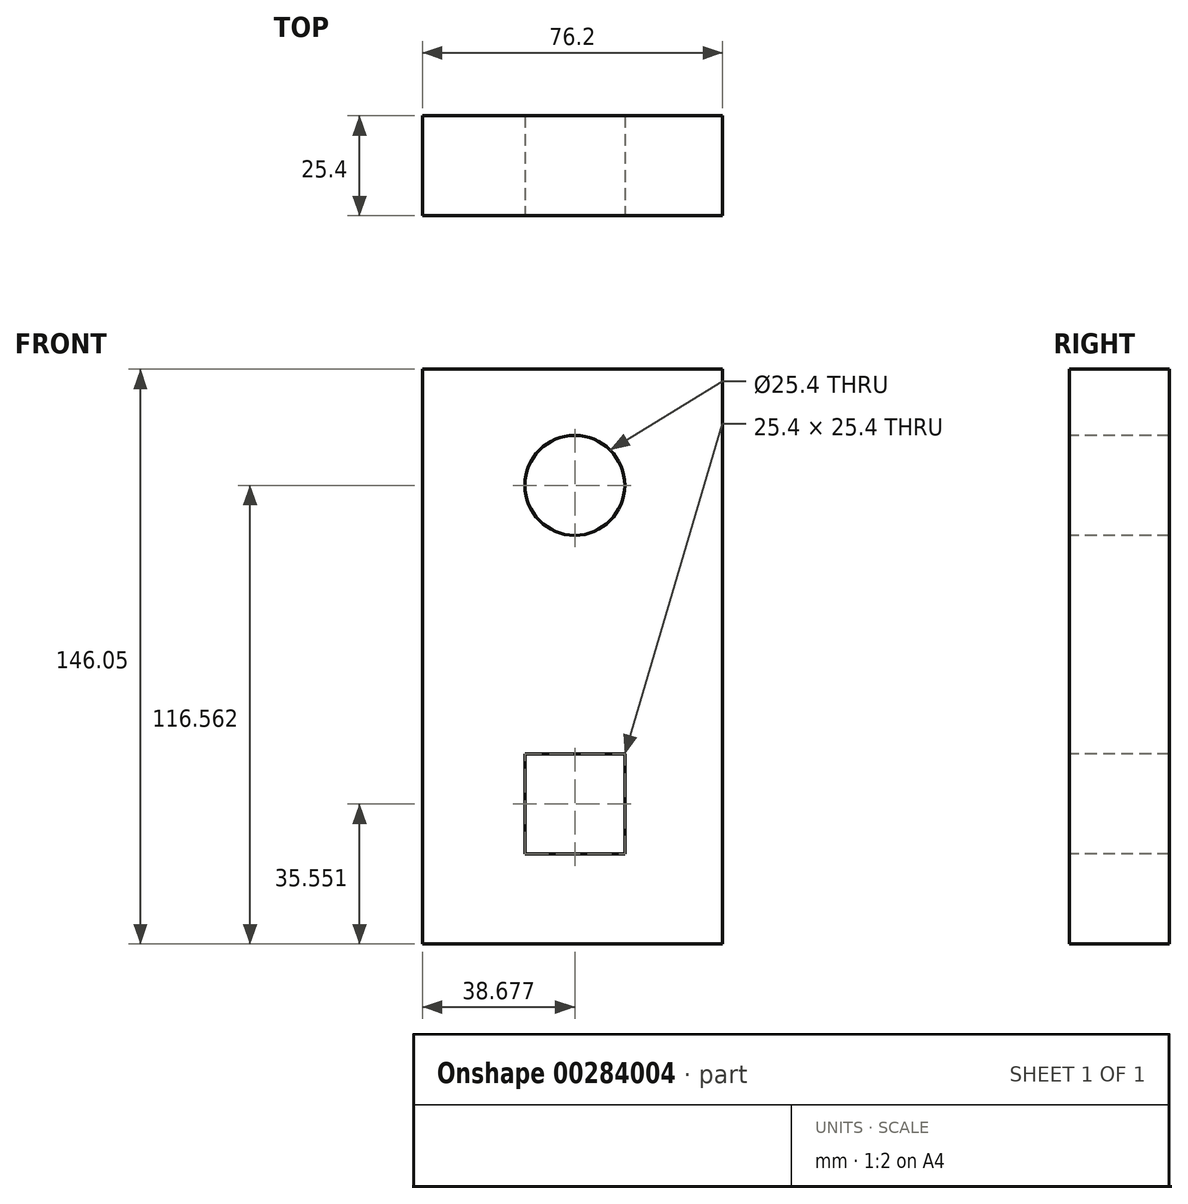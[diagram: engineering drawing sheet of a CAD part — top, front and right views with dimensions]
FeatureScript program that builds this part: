
annotation { "Feature Type Name" : "Feature", "Feature Type Description" : "" }
export const myFeature = defineFeature(function(context is Context, id is Id, definition is map)
    precondition{}
    {
        {
            var Q0;
            Q0=qCreatedBy(makeId("Front.planeOp"),FACE);
            var sketch = newSketch(context, id + "F0", { "sketchPlane" : qUnion([Q0])});
            skLineSegment(sketch, "E0", {"start": v(-38.38, 126) * mm, "end": v(-38.38, -20.05) * mm});
            skLineSegment(sketch, "E1", {"start": v(-38.38, -20.05) * mm, "end": v(37.82, -20.05) * mm});
            skLineSegment(sketch, "E2", {"start": v(37.82, -20.05) * mm, "end": v(37.82, 126) * mm});
            skLineSegment(sketch, "E3", {"start": v(37.82, 126) * mm, "end": v(-38.38, 126) * mm});
            skSolve(sketch);
        }
        {
            var Q0;
            Q0 = qSketchRegion(id + "F0", true);
            extrude(context, id + "F1", {"entities" : qUnion([Q0]), "depth" : 25.4 * mm});
        }
        {
            var Q0;
            Q0=makeQuery(id+"F1.opExtrude","CAP_FACE",FACE,{"disambiguationData":[OSD([sQuery(id+"F0.wireOp",EDGE,"E0"),sQuery(id+"F0.wireOp",EDGE,"E1"),sQuery(id+"F0.wireOp",EDGE,"E2"),sQuery(id+"F0.wireOp",EDGE,"E3")])],"isStart":false});
            var sketch = newSketch(context, id + "F2", { "sketchPlane" : qUnion([Q0])});
            skLineSegment(sketch, "E4.bottom", {"start": v(-12.4, 28.2) * mm, "end": v(13, 28.2) * mm});
            skLineSegment(sketch, "E4.top", {"start": v(-12.4, 2.8) * mm, "end": v(13, 2.8) * mm});
            skLineSegment(sketch, "E4.left", {"start": v(-12.4, 28.2) * mm, "end": v(-12.4, 2.8) * mm});
            skLineSegment(sketch, "E4.right", {"start": v(13, 28.2) * mm, "end": v(13, 2.8) * mm});
            skSolve(sketch);
        }
        {
            var Q0;
            Q0 = qSketchRegion(id + "F2", true);
            extrude(context, id + "F3", {"entities" : qUnion([Q0]), "operationType" : NewBodyOperationType.REMOVE, "oppositeDirection" : true, "depth" : 25.4 * mm});
        }
        {
            var Q0;
            Q0=makeQuery(id+"F1.opExtrude","CAP_FACE",FACE,{"disambiguationData":[OSD([sQuery(id+"F0.wireOp",EDGE,"E0"),sQuery(id+"F0.wireOp",EDGE,"E1"),sQuery(id+"F0.wireOp",EDGE,"E2"),sQuery(id+"F0.wireOp",EDGE,"E3")])],"isStart":false});
            var sketch = newSketch(context, id + "F4", { "sketchPlane" : qUnion([Q0])});
            skCircle(sketch, "E5", {"center": v(0.3, 96.51) * mm, "radius": 12.7 * mm});
            skSolve(sketch);
        }
        {
            var Q0;
            Q0 = qSketchRegion(id + "F4", true);
            extrude(context, id + "F5", {"entities" : qUnion([Q0]), "operationType" : NewBodyOperationType.REMOVE, "oppositeDirection" : true, "depth" : 25.4 * mm});
        }
    });
